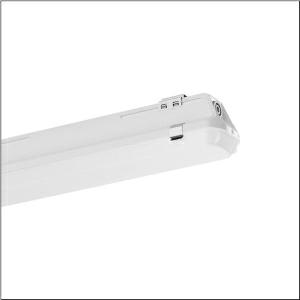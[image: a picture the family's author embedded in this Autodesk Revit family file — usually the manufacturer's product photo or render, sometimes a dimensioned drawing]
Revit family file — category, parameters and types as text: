
# Revit family: monsun_r__21_51fb207l420j_e717
name_source: partatom
category: Lighting Fixtures
units: mm (PartAtom-declared; Revit-internal decimal feet)

## family parameters
Cut with Voids When Loaded = No
Host = Face
Light Source = No
Part Type = Normal
Room Calculation Point = No
Round Connector Dimension = Use Diameter
Shared = No

## types (1)
- Monsun® 21 (1 x LED, 2620 lm, 19.3 W, 4000K)
    Apparent Load = 19 VA
    CIE Flux Codes = 45 75 93 94 100
    Color Rendering = 80
    Color Temperature = 4000K
    Default Elevation = 1800 mm
    Description = Monsun® 21, damp-proof luminaire, chain hanger, primary optical cover: enclosure, of PC, light emission: direct distribution, primary light characteristic: symmetric, installation type: suspended mounting, surface-mounted, horizontal mounting, vertical mounting, LED, rated luminous flux: 2.620lm, luminous efficacy: 138lm/W, light colour: 840, colour temperature: 4000K, control gear: ECG, with terminal, 3-pole, max. 2.5mm², mains connection: 220..240V, AC, 50/60Hz, rated input power: 19W, housing, of glass-fibre reinforced plastic, uncoated, bright grey, incl. chain hanger, length: 1.299mm, width: 90mm, height: 88mm, clip for enclosure, of stainless steel (V2A), ceiling mounting element, of stainless steel (V2A), chain hanger, of stainless steel (V2A), protection rating (complete): IP66, insulation class (complete): insulation class I (protective earthing), certification: CE, ENEC, VDE, UKCA, protection symbol: D, impact resistance: IK08, permissible operating ambient temperature: -25..+35°C, standard: EN 50419, EN 60598-2-1, corresponds to IFS (International Featured Standards) requirements for safety and quality in the food industry, for indoor or canopied outdoor use, no direct snow, no direct sun, no direct rain, contact your sales advisor before using the luminaires in applications with unclear chemical exposure, large temperature fluctuations or condensation-forming humidity, LABS conformity tested according to VDMA 24364:2018-05, packaging unit: 1 piece
    Height = 88 mm
    Lamp = 1 x LED
    Lamp Light Flux = 2620 lm
    Lamp Power = 19.3 W
    Lamp count = 1
    Length = 1299 mm
    Luminous efficacy = 136 lm/W
    Manufacturer = Siteco
    ModVariant = No
    Model = 51FB207L420J
    Mounting Place = Ceiling
    Mounting Type = Surface mounted
    Number of Poles = 1
    OnlyDefault = Yes
    Power Factor = 1
    Product Name = Monsun® 21
    Product group = damp-proof luminaire
    ProductGroupID = 300
    Protection Class = Protection class I
    Protection Degree = IP 66
    RLX_Detail_Level = 1
    RLX_Emergency_Light_Flux = 0 lm
    RLX_Emergency_Type = 0
    RLX_Emergency_Type_DB = No
    RlxData = <blob elided: 89769 chars, md5=48b1d0bc>
    Socket = socket
    Standby Power = 0 W
    System Light Flux = 2620 lm
    System Power = 19 W
    Type Comments = Product without accessories
    Type Image = l_1006717.jpg
    URL = http://relux.com
    VarID = ---
    Voltage = 0 V
    Weight = 0.00 kg
    Width = 90 mm

## geometry (parser evidence)
native form markers: Blend x4, Sweep x13
no freeform markers — native parametric forms only
